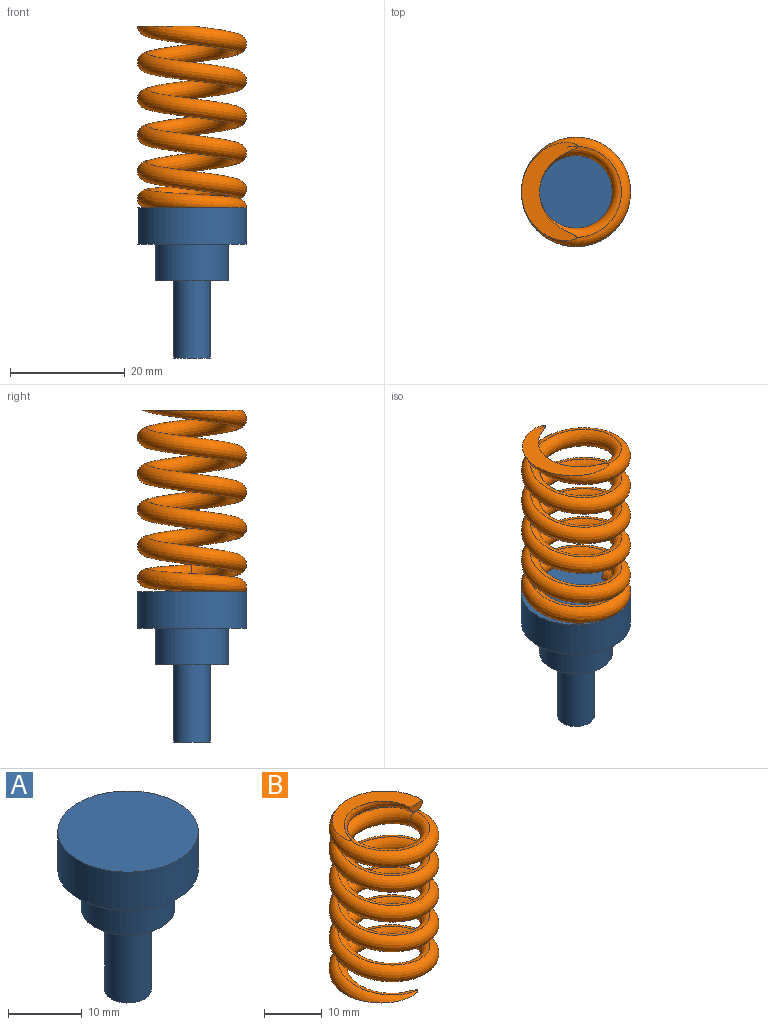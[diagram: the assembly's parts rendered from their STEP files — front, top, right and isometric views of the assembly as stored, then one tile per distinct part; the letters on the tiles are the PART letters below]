
ASSEMBLY  parts=2 mates=1
PART A: 7 faces, bbox 19.1x19.1x26.2 mm
  f0: cylinder r=9.53mm len=19.05mm, axis (0,0,1), area 380mm2, adj f1,f2
  f1: plane 19.05x19.05mm, normal (0,0,-1), area 158.3mm2, adj f0,f3
  f2: plane 19.05x19.05mm, normal (0,0,1), area 285mm2, adj f0
  f3: cylinder r=6.35mm len=12.7mm, axis (0,0,1), area 253.4mm2, adj f1,f4
  f4: plane 12.7x12.7mm, normal (0,0,-1), area 95mm2, adj f3,f5
  f5: cylinder r=3.17mm len=13.49mm, axis (0,0,1), area 269.2mm2, adj f4,f6
  f6: plane 6.35x6.35mm, normal (0,0,-1), area 31.7mm2, adj f5
PART B: 7 faces, bbox 24.2x24.2x38.7 mm
  f0: bspline ~33.69x22.37mm, area 1272.3mm2, adj f1,f2,f6
  f1: bspline ~33.69x15.98mm, area 988.2mm2, adj f0,f3,f6
  f2: bspline ~18.91x18.9mm, area 251mm2, adj f0,f3,f4,f5
  f3: bspline ~16.06x15.97mm, area 192.5mm2, adj f1,f2,f4,f5
  f4: plane 3.63x2.04mm, normal (0,-1,0), area 4mm2, adj f2,f3,f5
  f5: plane 19.62x11.11mm, normal (0,0,1), area 61.6mm2, adj f2,f3,f4
  f6: plane 18.65x11.3mm, normal (0,0,-1), area 63mm2, adj f0,f1
PLACE A at identity fixed
PLACE B rot(axis=(1,0,0),180deg) t=(0,0,25.4)mm
MATE fastened B.f5 <-> A.f0  axis (0,0,-1) through (0,0,25.4)mm
